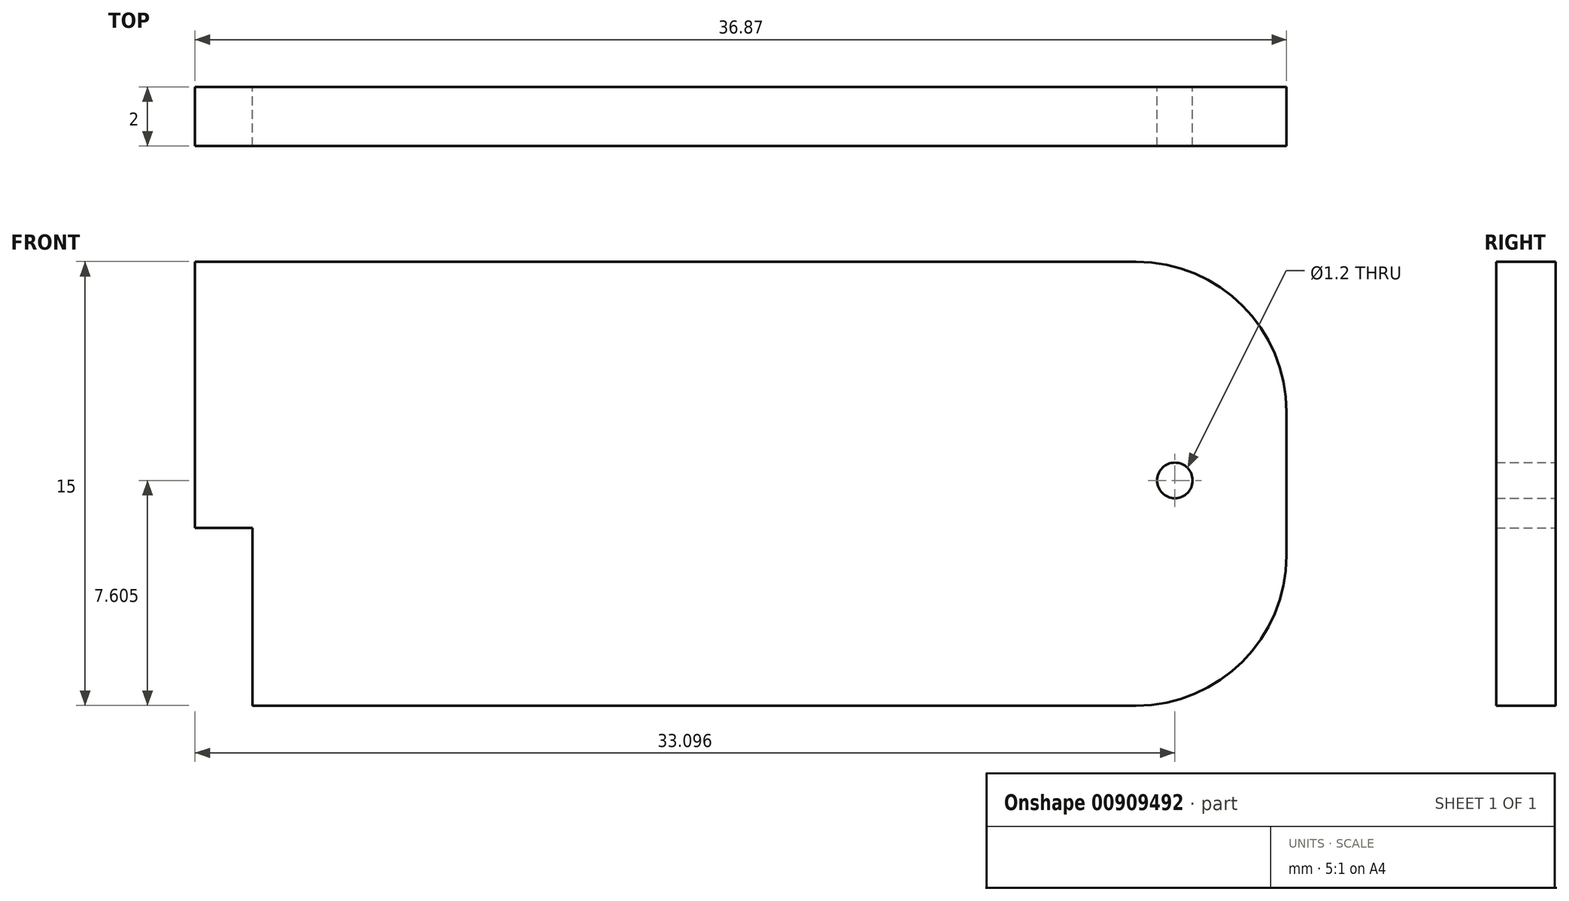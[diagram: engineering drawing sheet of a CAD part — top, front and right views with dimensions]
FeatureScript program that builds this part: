
annotation { "Feature Type Name" : "Feature", "Feature Type Description" : "" }
export const myFeature = defineFeature(function(context is Context, id is Id, definition is map)
    precondition{}
    {
        {
            var Q0;
            Q0=qCreatedBy(makeId("Front.planeOp"),FACE);
            var sketch = newSketch(context, id + "F0", { "sketchPlane" : qUnion([Q0])});
            skLineSegment(sketch, "E0.bottom", {"start": v(14.9, -7.87) * mm, "end": v(-12.12, -7.87) * mm});
            skLineSegment(sketch, "E0.top", {"start": v(14.9, 7.13) * mm, "end": v(-12.12, 7.13) * mm});
            skLineSegment(sketch, "E0.left", {"start": v(14.9, -7.87) * mm, "end": v(14.9, 7.13) * mm});
            skLineSegment(sketch, "E0.right", {"start": v(-12.12, -7.87) * mm, "end": v(-12.12, 7.13) * mm});
            skLineSegment(sketch, "E1.bottom", {"start": v(14.9, -7.87) * mm, "end": v(22.8, -7.87) * mm});
            skLineSegment(sketch, "E1.top", {"start": v(14.9, 7.13) * mm, "end": v(22.8, 7.13) * mm});
            skLineSegment(sketch, "E1.right", {"start": v(22.8, -7.87) * mm, "end": v(22.8, 7.13) * mm});
            skLineSegment(sketch, "E2.bottom", {"start": v(-12.12, -1.87) * mm, "end": v(-14.06, -1.87) * mm});
            skLineSegment(sketch, "E2.top", {"start": v(-12.12, 7.13) * mm, "end": v(-14.06, 7.13) * mm});
            skLineSegment(sketch, "E2.left", {"start": v(-12.12, -1.87) * mm, "end": v(-12.12, 7.13) * mm});
            skLineSegment(sketch, "E2.right", {"start": v(-14.06, -1.87) * mm, "end": v(-14.06, 7.13) * mm});
            skPoint(sketch, "E3", {"position": v(19.04, -0.27) * mm});
            skSolve(sketch);
        }
        {
            var Q0;
            Q0=makeQuery(id+"F0.imprint","IMPRINT",FACE,{"disambiguationData":[TD([[makeQuery(id+"F0.imprint","IMPRINT",EDGE,{"derivedFrom":sQuery(id+"F0.wireOp",EDGE,"E0.left")}),-1.0]])]});
            var Q1;
            {var subQ3=sQuery(id+"F0.wireOp",EDGE,"E0.bottom");Q1=makeQuery(id+"F0.imprint","IMPRINT",FACE,{"disambiguationData":[TD([[makeQuery(id+"F0.imprint","IMPRINT",EDGE,{"derivedFrom":subQ3}),-1.0]])]});}
            var Q2;
            {var subQ2=sQuery(id+"F0.wireOp",EDGE,"E2.bottom");Q2=makeQuery(id+"F0.imprint","IMPRINT",FACE,{"disambiguationData":[TD([[makeQuery(id+"F0.imprint","IMPRINT",EDGE,{"derivedFrom":subQ2}),-1.0]])]});}
            extrude(context, id + "F1", {"entities" : qUnion([Q0, Q1, Q2]), "depth" : 2 * mm, "offsetDistance" : 25.4 * mm});
        }
        {
            var Q0;
            Q0=makeQuery(id+"F1.opExtrude","SWEPT_EDGE",EDGE,{"disambiguationData":[OSD([sQuery(id+"F0.wireOp",EDGE,"E1.bottom"),sQuery(id+"F0.wireOp",EDGE,"E1.right")])]});
            var Q1;
            Q1=makeQuery(id+"F1.opExtrude","SWEPT_EDGE",EDGE,{"disambiguationData":[OSD([sQuery(id+"F0.wireOp",EDGE,"E1.top"),sQuery(id+"F0.wireOp",EDGE,"E1.right")])]});
            fillet(context, id + "F2", {"entities" : qUnion([Q0, Q1]), "radius" : 5.08 * mm, "tangentPropagation" : true, "allowEdgeOverflow" : false});
        }
        {
            var Q0;
            Q0=sQuery(id+"F0.wireOp",VERTEX,"E3");
            var Q1;
            Q1=makeQuery(id+"F1.opExtrude","SWEPT_BODY",BODY,{"disambiguationData":[OSD([sQuery(id+"F0.wireOp",EDGE,"E0.bottom"),sQuery(id+"F0.wireOp",EDGE,"E0.top"),sQuery(id+"F0.wireOp",EDGE,"E0.right"),sQuery(id+"F0.wireOp",EDGE,"E1.bottom"),sQuery(id+"F0.wireOp",EDGE,"E1.top"),sQuery(id+"F0.wireOp",EDGE,"E1.right"),sQuery(id+"F0.wireOp",EDGE,"E2.bottom"),sQuery(id+"F0.wireOp",EDGE,"E2.top"),sQuery(id+"F0.wireOp",EDGE,"E2.right")])]});
            hole(context, id + "F3", {"style" : HoleStyle.SIMPLE, "endStyle" : HoleEndStyle.BLIND, "oppositeDirection" : true, "holeDiameter" : 1.2 * mm, "majorDiameter" : 6.35 * mm, "holeDepth" : 12.7 * mm, "isTappedThrough" : true, "tappedDepth" : 12.7 * mm, "tapClearance" : 3, "locations" : qUnion([Q0]), "scope" : qUnion([Q1])});
        }
    });
